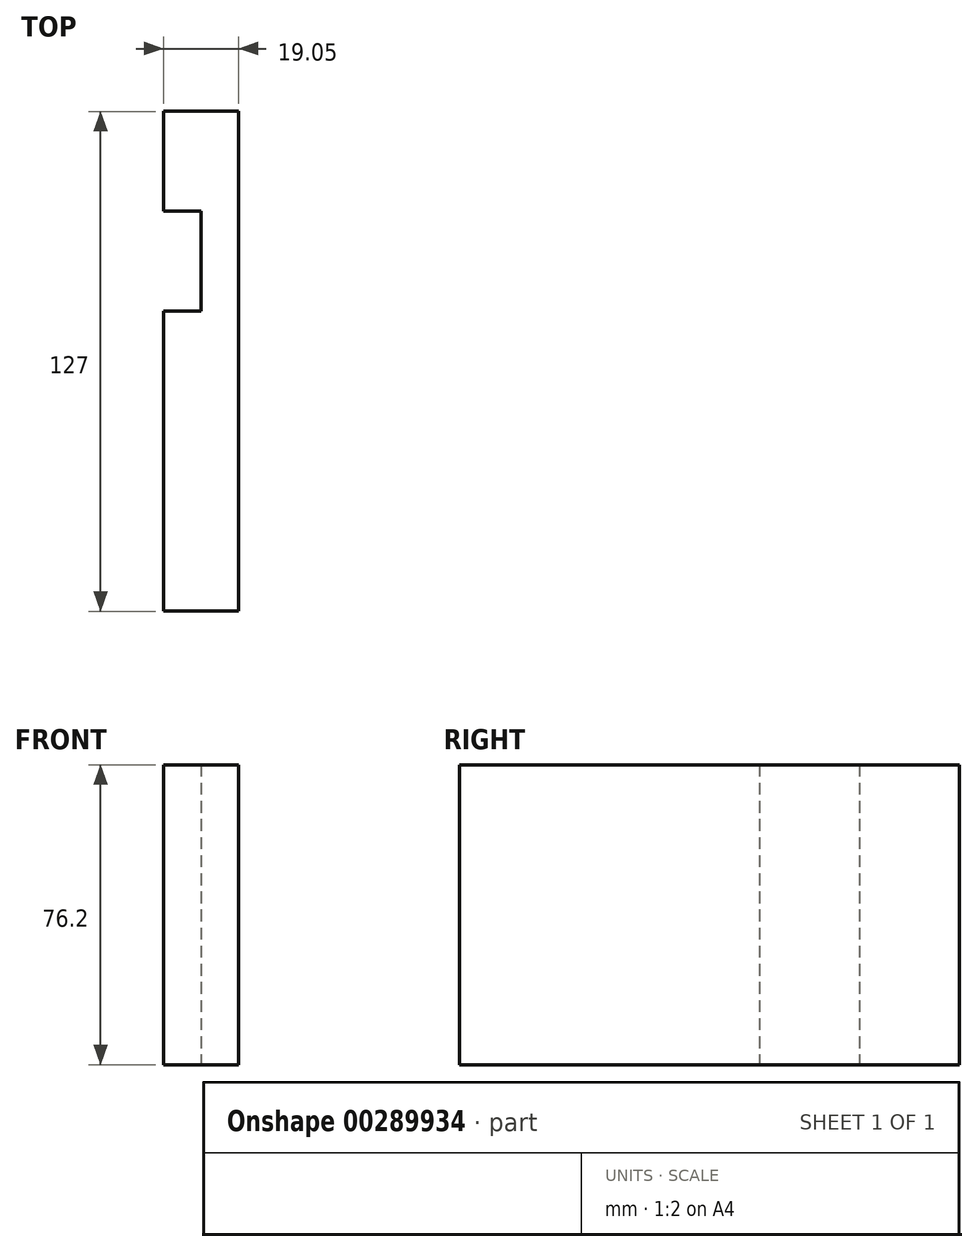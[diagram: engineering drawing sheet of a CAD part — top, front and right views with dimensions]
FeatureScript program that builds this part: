
annotation { "Feature Type Name" : "Feature", "Feature Type Description" : "" }
export const myFeature = defineFeature(function(context is Context, id is Id, definition is map)
    precondition{}
    {
        {
            var Q0;
            Q0=qCreatedBy(makeId("Top.planeOp"),FACE);
            var sketch = newSketch(context, id + "F0", { "sketchPlane" : qUnion([Q0])});
            skLineSegment(sketch, "E0.bottom", {"start": v(-19.05, 96.8) * mm, "end": v(0, 96.8) * mm});
            skLineSegment(sketch, "E0.top", {"start": v(-19.05, -30.2) * mm, "end": v(0, -30.2) * mm});
            skLineSegment(sketch, "E0.left", {"start": v(-19.05, 96.8) * mm, "end": v(-19.05, 71.4) * mm});
            skLineSegment(sketch, "E0.right", {"start": v(0, 96.8) * mm, "end": v(0, -30.2) * mm});
            skLineSegment(sketch, "E1", {"start": v(-19.05, 71.4) * mm, "end": v(-9.53, 71.4) * mm});
            skLineSegment(sketch, "E2", {"start": v(-9.53, 71.4) * mm, "end": v(-9.53, 46) * mm});
            skLineSegment(sketch, "E3", {"start": v(-9.53, 46) * mm, "end": v(-19.05, 46) * mm});
            skLineSegment(sketch, "E4.trimOffspring", {"start": v(-19.05, 46) * mm, "end": v(-19.05, -30.2) * mm});
            skSolve(sketch);
        }
        {
            var Q0;
            Q0 = qSketchRegion(id + "F0", true);
            extrude(context, id + "F1", {"entities" : qUnion([Q0]), "depth" : 76.2 * mm});
        }
    });
